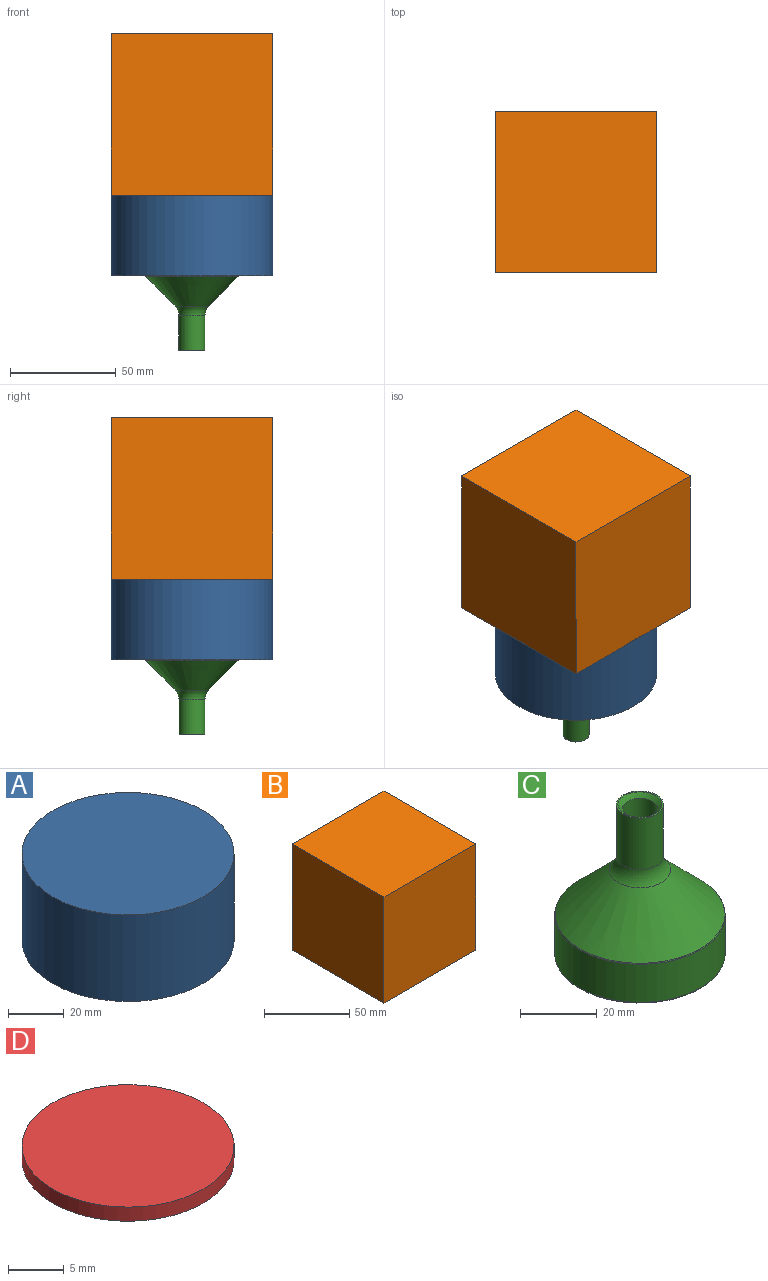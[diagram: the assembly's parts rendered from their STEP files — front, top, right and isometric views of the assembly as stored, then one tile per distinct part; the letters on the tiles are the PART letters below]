
ASSEMBLY  parts=4 mates=3
PART A: 5 faces, bbox 76.2x76.2x38.1 mm
  f0: plane 76.2x76.2mm, normal (0,0,1), area 4560.4mm2, adj f4
  f1: plane 44.45x44.45mm, normal (0,0,-1), area 1551.8mm2, adj f2
  f2: cylinder r=22.23mm len=44.45mm, axis (0,0,-1), area 1773.5mm2, adj f1,f3
  f3: plane 76.2x76.2mm, normal (0,0,-1), area 3008.6mm2, adj f2,f4
  f4: cylinder r=38.1mm len=76.2mm, axis (0,0,-1), area 9120.7mm2, adj f0,f3
PART B: 6 faces, bbox 76.2x76.2x76.2 mm
  f0: plane 76.2x76.2mm, normal (0,1,0), area 5806.4mm2, adj f1,f3,f4,f5
  f1: plane 76.2x76.2mm, normal (-1,0,0), area 5806.4mm2, adj f0,f2,f4,f5
  f2: plane 76.2x76.2mm, normal (0,-1,0), area 5806.4mm2, adj f1,f3,f4,f5
  f3: plane 76.2x76.2mm, normal (1,0,0), area 5806.4mm2, adj f0,f2,f4,f5
  f4: plane 76.2x76.2mm, normal (0,0,1), area 5806.4mm2, adj f0,f1,f2,f3
  f5: plane 76.2x76.2mm, normal (0,0,-1), area 5806.4mm2, adj f0,f1,f2,f3
PART C: 13 faces, bbox 48.1x48.1x47.8 mm
  f0: torus R=12.49mm, axis (0,0,-1), area 212.1mm2, adj f1,f11
  f1: cylinder r=6.14mm len=16.42mm, axis (0,0,-1), area 633.1mm2, adj f0,f2
  f2: plane 12.27x12.27mm, normal (0,0,1), area 14.9mm2, adj f1,f12
  f3: cylinder r=4.54mm len=43.44mm, axis (0,0,-1), area 1238.3mm2, adj f4,f12
  f4: plane 19.05x19.05mm, normal (0,0,-1), area 220.4mm2, adj f3,f5
  f5: cylinder r=9.53mm len=19.05mm, axis (0,0,-1), area 95.8mm2, adj f4,f6
  f6: plane 19.05x19.05mm, normal (0,0,1), area 285mm2, adj f5
  f7: plane 43.65x43.65mm, normal (0,0,-1), area 1496.4mm2, adj f8
  f8: torus R=21.82mm, axis (0,0,-1), area 87.2mm2, adj f7,f9
  f9: cylinder r=22.23mm len=44.45mm, axis (0,0,-1), area 1694.5mm2, adj f8,f10
  f10: torus R=21.82mm, axis (0,0,-1), area 43.8mm2, adj f9,f11
  f11: cone r=22.11mm half-angle=45deg, axis (0,0,-1), area 1887.4mm2, adj f0,f10
  f12: cone r=5.74mm half-angle=45deg, axis (0,0,1), area 54.8mm2, adj f2,f3
PART D: 3 faces, bbox 19.1x19.1x1.6 mm
  f0: cylinder r=9.53mm len=19.05mm, axis (0,0,-1), area 93.1mm2, adj f1,f2
  f1: plane 19.05x19.05mm, normal (0,0,1), area 285mm2, adj f0
  f2: plane 19.05x19.05mm, normal (0,0,-1), area 285mm2, adj f0
PLACE A rot(axis=(-1,0,0),0deg) t=(0,0.35,-12.82)mm
PLACE B rot(axis=(-1,0,0),0deg) t=(0,0.35,25.28)mm
PLACE C rot(axis=(1,0,0),180deg) t=(0,0.35,-0.12)mm fixed
PLACE D rot(axis=(-1,0,0),0deg) t=(0,0.35,-3.28)mm
MATE fastened D.f0 <-> C.f0  axis (0,0,1) through (0,0.35,-1.72)mm
MATE fastened A.f2 <-> C.f0  axis (0,0,-1) through (0,0.35,-0.12)mm
MATE fastened B.f5 <-> A.f2  axis (0,0,-1) through (0,0.35,25.28)mm
